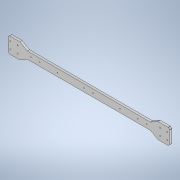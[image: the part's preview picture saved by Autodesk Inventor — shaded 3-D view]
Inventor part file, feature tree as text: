
AUTODESK INVENTOR PART (.ipt)
format: ipt  version: 2022 (Build 260153000, 153)  size: 133,120 bytes
history: imported  units: in
note: dims shown in document units (in); Inventor stores cm internally (conversion verified against a paired STEP export)
features: imported_body x1
ambient origin geometry x8: Origin, YZ Plane, XZ Plane, XY Plane, X Axis, Y Axis, Z Axis, Center Point
bodies: Solid1 (imported_parasolid), Body1 (imported_parasolid)
feature tree (1):
  imported_body  NMx_Import_Brep_tag  [imported B-rep: ~42 faces, bbox_mm=[453.0, 44.0, 6.35]]
